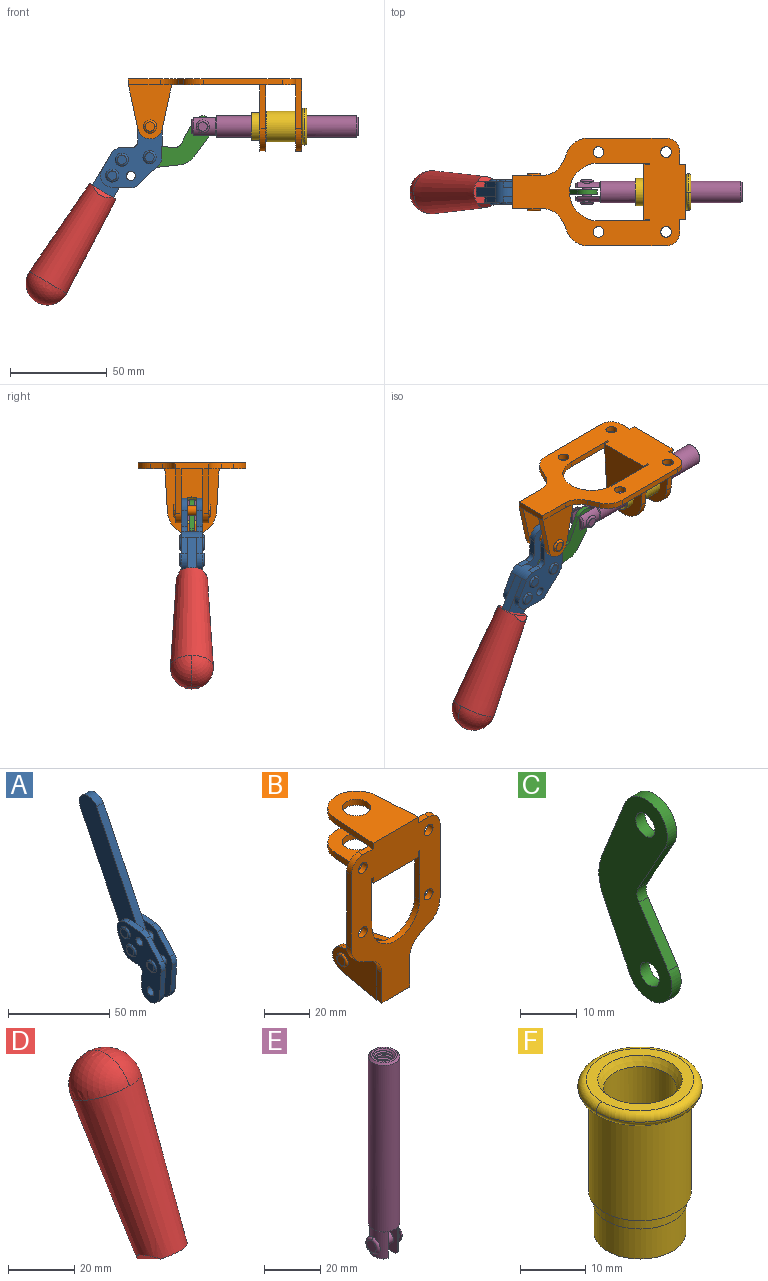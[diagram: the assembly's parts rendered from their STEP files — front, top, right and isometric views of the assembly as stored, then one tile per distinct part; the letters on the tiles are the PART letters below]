
ASSEMBLY  parts=6 mates=6
PART A: 59 faces, bbox 12.9x60.2x99.6 mm
  f0: torus R=2.39mm, axis (-1,0,0), area 14.9mm2, adj f20,f43,f51
  f1: torus R=2.39mm, axis (-1,0,0), area 14.9mm2, adj f19,f42,f51
  f2: torus R=2.39mm, axis (-1,0,0), area 14.9mm2, adj f18,f35,f51
  f3: torus R=2.39mm, axis (-1,0,0), area 14.9mm2, adj f14,f17,f23
  f4: torus R=2.39mm, axis (-1,0,0), area 14.9mm2, adj f13,f16,f23
  f5: torus R=2.39mm, axis (-1,0,0), area 14.9mm2, adj f12,f15,f23
  f6: cylinder r=2.39mm len=4.78mm, axis (1,0,0), area 46.5mm2, adj f48,f50,f51
  f7: cylinder r=2.39mm len=4.78mm, axis (1,0,0), area 46.5mm2, adj f50,f51
  f8: cylinder r=6.35mm len=12.68mm, axis (1,0,0), area 61.8mm2, adj f38,f39,f50,f51
  f9: cylinder r=2.39mm len=4.78mm, axis (-1,0,0), area 70.5mm2, adj f46,f50
  f10: cylinder r=2.39mm len=4.78mm, axis (-1,0,0), area 46.5mm2, adj f23,f45,f46
  f11: cylinder r=2.39mm len=4.78mm, axis (-1,0,0), area 46.5mm2, adj f23,f46
  f12: plane 4.78x4.78mm, normal (1,0,0), area 17.9mm2, adj f5,f15
  f13: plane 4.78x4.78mm, normal (1,0,0), area 17.9mm2, adj f4,f16
  f14: plane 4.78x4.78mm, normal (1,0,0), area 17.9mm2, adj f3,f17
  f15: torus R=2.39mm, axis (-1,0,0), area 14.9mm2, adj f5,f12,f23
  f16: torus R=2.39mm, axis (-1,0,0), area 14.9mm2, adj f4,f13,f23
  f17: torus R=2.39mm, axis (-1,0,0), area 14.9mm2, adj f3,f14,f23
  f18: plane 4.78x4.78mm, normal (-1,0,0), area 17.9mm2, adj f2,f35
  f19: plane 4.78x4.78mm, normal (-1,0,0), area 17.9mm2, adj f1,f42
  f20: plane 4.78x4.78mm, normal (-1,0,0), area 17.9mm2, adj f0,f43
  f21: plane 2.26x0.2mm, normal (1,0,0), area 0.2mm2, adj f31,f44
  f22: plane 2.26x0.2mm, normal (-1,0,0), area 0.2mm2, adj f41,f44
  f23: plane 39.37x30.77mm, normal (1,0,0), area 565.5mm2, adj f3,f4,f5,f10,f11,f15,f16,f17
  f24: cylinder r=6.1mm len=4.15mm, axis (-1,0,0), area 14.7mm2, adj f23,f25,f32,f46
  f25: plane 10.25x9.01mm, normal (0,-0.75,0.66), area 42.3mm2, adj f23,f24,f26,f46
  f26: cylinder r=6.35mm len=4.64mm, axis (-1,0,0), area 15.6mm2, adj f23,f25,f27,f46
  f27: plane 15.84x3.1mm, normal (0,-1,-0.07), area 49.2mm2, adj f23,f26,f28,f46
  f28: cylinder r=6.35mm len=12.68mm, axis (-1,0,0), area 61.8mm2, adj f23,f27,f29,f46
  f29: plane 8.11x3.1mm, normal (0,1,0.07), area 25.2mm2, adj f23,f28,f30,f46
  f30: cylinder r=3.05mm len=3.25mm, axis (-1,0,0), area 14.8mm2, adj f23,f29,f31,f46
  f31: plane 5.99x3.1mm, normal (0,0.07,-1), area 18.6mm2, adj f21,f23,f30,f44,f46
  f32: plane 9.5x3.1mm, normal (0,-0.07,1), area 29.5mm2, adj f23,f24,f33,f46,f47
  f33: cylinder r=6.1mm len=8.63mm, axis (-1,0,0), area 39.1mm2, adj f23,f32,f34,f47
  f34: plane 8.65x3.96mm, normal (0,0.91,-0.42), area 29.5mm2, adj f23,f33,f44,f47
  f35: torus R=2.39mm, axis (-1,0,0), area 14.9mm2, adj f2,f18,f51
  f36: plane 10.25x9.01mm, normal (0,-0.75,0.66), area 42.3mm2, adj f37,f49,f50,f51
  f37: cylinder r=6.35mm len=4.64mm, axis (1,0,0), area 15.6mm2, adj f36,f38,f50,f51
  f38: plane 15.84x3.1mm, normal (0,-1,-0.07), area 49.2mm2, adj f8,f37,f50,f51
  f39: plane 8.11x3.1mm, normal (0,1,0.07), area 25.2mm2, adj f8,f40,f50,f51
  f40: cylinder r=3.05mm len=3.25mm, axis (1,0,0), area 14.8mm2, adj f39,f41,f50,f51
  f41: plane 5.99x3.1mm, normal (0,0.07,-1), area 18.6mm2, adj f22,f40,f44,f50,f51
  f42: torus R=2.39mm, axis (-1,0,0), area 14.9mm2, adj f1,f19,f51
  f43: torus R=2.39mm, axis (-1,0,0), area 14.9mm2, adj f0,f20,f51
  f44: cylinder r=6.35mm len=12.12mm, axis (-1,0,0), area 128.9mm2, adj f21,f22,f23,f31,f34,f41,f46,f47
  f45: plane 2.65x1.35mm, normal (1,0,0), area 1mm2, adj f10,f55
  f46: plane 39.08x20.42mm, normal (-1,0,0), area 412.5mm2, adj f9,f10,f11,f24,f25,f26,f27,f28
  f47: plane 77.62x39.82mm, normal (1,0,0), area 850mm2, adj f32,f33,f34,f44,f53,f54,f55
  f48: plane 2.65x1.35mm, normal (-1,0,0), area 1mm2, adj f6,f55
  f49: cylinder r=6.1mm len=4.15mm, axis (1,0,0), area 14.7mm2, adj f36,f50,f51,f56
  f50: plane 39.08x20.42mm, normal (1,0,0), area 412.5mm2, adj f6,f7,f8,f9,f36,f37,f38,f39
  f51: plane 39.37x30.77mm, normal (-1,0,0), area 565.5mm2, adj f0,f1,f2,f6,f7,f8,f35,f36
  f52: plane 8.65x3.96mm, normal (0,0.91,-0.42), area 29.5mm2, adj f44,f51,f57,f58
  f53: plane 68.49x33.4mm, normal (0,0.9,-0.44), area 358.1mm2, adj f44,f47,f54,f58
  f54: cylinder r=6.35mm len=12.06mm, axis (1,0,0), area 93.7mm2, adj f47,f53,f55,f58
  f55: plane 68.49x33.4mm, normal (0,-0.9,0.44), area 358.1mm2, adj f44,f45,f46,f47,f48,f50,f54,f58
  f56: plane 9.5x3.1mm, normal (0,-0.07,1), area 29.5mm2, adj f49,f50,f51,f57,f58
  f57: cylinder r=6.1mm len=8.63mm, axis (1,0,0), area 39.1mm2, adj f51,f52,f56,f58
  f58: plane 77.62x39.82mm, normal (-1,0,0), area 850mm2, adj f44,f52,f53,f54,f55,f56,f57
PART B: 55 faces, bbox 55.7x37.4x89.8 mm
  f0: torus R=2.41mm, axis (-1,0,0), area 15mm2, adj f11,f15,f25
  f1: torus R=2.41mm, axis (-1,0,0), area 15mm2, adj f10,f12,f22
  f2: cylinder r=2.78mm len=5.56mm, axis (0,-1,0), area 54.2mm2, adj f30,f54
  f3: cylinder r=14.99mm len=29.97mm, axis (0,-1,0), area 145.9mm2, adj f30,f49,f53,f54
  f4: cylinder r=2.78mm len=5.56mm, axis (0,-1,0), area 54.2mm2, adj f30,f54
  f5: cylinder r=2.78mm len=5.56mm, axis (0,-1,0), area 54.2mm2, adj f30,f54
  f6: cylinder r=2.78mm len=5.56mm, axis (0,-1,0), area 54.2mm2, adj f30,f54
  f7: cylinder r=6.35mm len=12.7mm, axis (0,0,1), area 123.6mm2, adj f27,f51
  f8: cylinder r=6.35mm len=12.7mm, axis (0,0,-1), area 124.7mm2, adj f21,f35
  f9: cylinder r=2.41mm len=11.18mm, axis (-1,0,0), area 169.4mm2, adj f16,f19
  f10: plane 4.83x4.83mm, normal (1,0,0), area 18.3mm2, adj f1,f12
  f11: plane 4.83x4.83mm, normal (-1,0,0), area 18.3mm2, adj f0,f15
  f12: torus R=2.41mm, axis (-1,0,0), area 15mm2, adj f1,f10,f22
  f13: cylinder r=6.35mm len=12.41mm, axis (1,0,0), area 53.4mm2, adj f18,f19,f22,f23
  f14: cylinder r=6.35mm len=12.41mm, axis (-1,0,0), area 53.4mm2, adj f16,f17,f24,f25
  f15: torus R=2.41mm, axis (-1,0,0), area 15mm2, adj f0,f11,f25
  f16: plane 27.86x22.35mm, normal (1,0,0), area 425.4mm2, adj f9,f14,f17,f24,f30
  f17: plane 22.86x4.97mm, normal (0,0.21,0.98), area 72.5mm2, adj f14,f16,f25,f30
  f18: plane 22.86x4.97mm, normal (0,0.21,0.98), area 72.5mm2, adj f13,f19,f22,f30
  f19: plane 27.86x22.35mm, normal (-1,0,0), area 425.4mm2, adj f9,f13,f18,f23,f30
  f20: cylinder r=12.7mm len=25.35mm, axis (0,0,-1), area 119.8mm2, adj f21,f34,f35,f36
  f21: plane 34.21x28.07mm, normal (0,0,-1), area 702.4mm2, adj f8,f20,f30,f34,f36
  f22: plane 27.96x22.45mm, normal (1,0,0), area 407.2mm2, adj f1,f12,f13,f18,f23,f30,f42,f43
  f23: plane 22.86x4.97mm, normal (0,0.21,-0.98), area 72.5mm2, adj f13,f19,f22,f44
  f24: plane 22.86x4.97mm, normal (0,0.21,-0.98), area 72.5mm2, adj f14,f16,f25,f44
  f25: plane 27.86x22.35mm, normal (-1,0,0), area 407.1mm2, adj f0,f14,f15,f17,f24,f30,f45,f46
  f26: plane 3.1x0.95mm, normal (0,0,-1), area 2.7mm2, adj f30,f49,f50,f54
  f27: plane 34.21x28.07mm, normal (0,0,1), area 702.4mm2, adj f7,f28,f30,f50,f52
  f28: cylinder r=12.7mm len=25.35mm, axis (0,0,1), area 118.8mm2, adj f27,f50,f51,f52
  f29: plane 3.1x0.95mm, normal (0,0,-1), area 2.7mm2, adj f30,f52,f53,f54
  f30: plane 86.54x55.63mm, normal (0,1,0), area 2362.9mm2, adj f2,f3,f4,f5,f6,f16,f17,f18
  f31: plane 40.56x3.1mm, normal (-1,0,0), area 125.7mm2, adj f30,f32,f48,f54
  f32: cylinder r=7.11mm len=7.11mm, axis (0,-1,0), area 34.6mm2, adj f30,f31,f33,f54
  f33: plane 6.67x3.1mm, normal (0,0,1), area 20.4mm2, adj f30,f32,f34,f54
  f34: plane 25.39x3.13mm, normal (-1,0.06,0), area 79.5mm2, adj f20,f21,f33,f35,f54
  f35: plane 37.31x28.45mm, normal (0,0,1), area 789.9mm2, adj f8,f20,f34,f36,f54
  f36: plane 25.39x3.13mm, normal (1,0.06,0), area 79.5mm2, adj f20,f21,f35,f37,f54
  f37: plane 6.67x3.1mm, normal (0,0,1), area 20.4mm2, adj f30,f36,f38,f54
  f38: cylinder r=7.11mm len=7.11mm, axis (0,-1,0), area 34.6mm2, adj f30,f37,f39,f54
  f39: plane 40.56x3.1mm, normal (1,0,0), area 125.7mm2, adj f30,f38,f40,f54
  f40: cylinder r=11.18mm len=10.16mm, axis (0,-1,0), area 39.5mm2, adj f30,f39,f41,f54
  f41: plane 6.09x3.1mm, normal (0.42,0,-0.91), area 20.8mm2, adj f30,f40,f42,f54
  f42: cylinder r=11.18mm len=9.41mm, axis (0,-1,0), area 37.2mm2, adj f22,f30,f41,f43,f54
  f43: plane 16.5x3.1mm, normal (1,0,0), area 51.1mm2, adj f22,f42,f44,f54
  f44: plane 17.37x3.1mm, normal (0,0,-1), area 53.8mm2, adj f23,f24,f30,f43,f45,f54
  f45: plane 16.5x3.1mm, normal (-1,0,0), area 51.1mm2, adj f25,f44,f46,f54
  f46: cylinder r=11.18mm len=9.41mm, axis (0,-1,0), area 37.2mm2, adj f25,f30,f45,f47,f54
  f47: plane 6.09x3.1mm, normal (-0.42,0,-0.91), area 20.8mm2, adj f30,f46,f48,f54
  f48: cylinder r=11.18mm len=10.16mm, axis (0,-1,0), area 39.5mm2, adj f30,f31,f47,f54
  f49: plane 26.54x3.1mm, normal (-1,0,0), area 82.3mm2, adj f3,f26,f30,f54
  f50: plane 25.39x3.1mm, normal (1,0.06,0), area 78.8mm2, adj f26,f27,f28,f51,f54
  f51: plane 37.31x28.45mm, normal (0,0,-1), area 789.9mm2, adj f7,f28,f50,f52,f54
  f52: plane 25.39x3.1mm, normal (-1,0.06,0), area 78.8mm2, adj f27,f28,f29,f51,f54
  f53: plane 26.54x3.1mm, normal (1,0,0), area 82.3mm2, adj f3,f29,f30,f54
  f54: plane 89.66x55.63mm, normal (0,-1,0), area 2678.5mm2, adj f2,f3,f4,f5,f6,f26,f29,f31
PART C: 12 faces, bbox 2.3x18.2x42.8 mm
  f0: cylinder r=2.4mm len=4.8mm, axis (1,0,0), area 34.9mm2, adj f4,f11
  f1: cylinder r=10.41mm len=8.47mm, axis (1,0,0), area 20.2mm2, adj f4,f9,f10,f11
  f2: cylinder r=3.05mm len=3.16mm, axis (1,0,0), area 7.7mm2, adj f4,f6,f7,f11
  f3: cylinder r=2.4mm len=4.8mm, axis (1,0,0), area 34.9mm2, adj f4,f11
  f4: plane 42.81x18.23mm, normal (-1,0,0), area 414.1mm2, adj f0,f1,f2,f3,f5,f6,f7,f8
  f5: cylinder r=5.54mm len=10.67mm, axis (1,0,0), area 41.8mm2, adj f4,f6,f10,f11
  f6: plane 11.66x6.53mm, normal (0,-0.87,-0.49), area 30.9mm2, adj f2,f4,f5,f11
  f7: plane 11.17x7.33mm, normal (0,-0.84,0.55), area 30.9mm2, adj f2,f4,f8,f11
  f8: cylinder r=5.54mm len=10.51mm, axis (1,0,0), area 41.8mm2, adj f4,f7,f9,f11
  f9: plane 13.67x6.67mm, normal (0,0.9,-0.44), area 35.1mm2, adj f1,f4,f8,f11
  f10: plane 14.1x5.7mm, normal (0,0.93,0.37), area 35.1mm2, adj f1,f4,f5,f11
  f11: plane 42.81x18.23mm, normal (1,0,0), area 414.1mm2, adj f0,f1,f2,f3,f5,f6,f7,f8
PART D: 11 faces, bbox 22.3x42.6x64.5 mm
  f0: sphere r=11.13mm, area 411.4mm2, adj f1,f8
  f1: cone r=11.11mm half-angle=3.3deg, axis (0,0.44,0.9), area 3251.8mm2, adj f0,f7,f8,f9,f10
  f2: cylinder r=6.16mm len=11.7mm, axis (1,0,0), area 89.5mm2, adj f3,f4,f5,f6
  f3: plane 60.23x36.75mm, normal (-1,0,0), area 763.6mm2, adj f2,f4,f6,f10
  f4: plane 51.37x25.05mm, normal (0,0.9,-0.44), area 264.2mm2, adj f2,f3,f5,f10
  f5: plane 60.23x36.75mm, normal (1,0,0), area 763.6mm2, adj f2,f4,f6,f10
  f6: plane 51.37x25.05mm, normal (0,-0.9,0.44), area 264.2mm2, adj f2,f3,f5,f10
  f7: plane 9.95x5.95mm, normal (0.71,-0.31,-0.64), area 25.8mm2, adj f1,f10
  f8: sphere r=11.13mm, area 411.4mm2, adj f0,f1
  f9: plane 9.95x5.95mm, normal (-0.71,-0.31,-0.64), area 25.8mm2, adj f1,f10
  f10: plane 14.27x11.38mm, normal (0,-0.44,-0.9), area 106.7mm2, adj f1,f3,f4,f5,f6,f7,f9
PART E: 48 faces, bbox 12.6x11.1x86.1 mm
  f0: torus R=2.41mm, axis (-1,0,0), area 15mm2, adj f30,f32,f34
  f1: torus R=2.41mm, axis (-1,0,0), area 15mm2, adj f29,f31,f33
  f2: cylinder r=5.54mm len=72.39mm, axis (0,0,1), area 2518.5mm2, adj f3,f4,f42,f43
  f3: cone r=5.54mm half-angle=45deg, axis (0,0,1), area 7.6mm2, adj f2,f5,f41
  f4: cone r=5.54mm half-angle=45deg, axis (0,0,-1), area 34.9mm2, adj f2,f39
  f5: cylinder r=5.08mm len=11.48mm, axis (0,0,1), area 108.3mm2, adj f3,f7,f8,f41
  f6: cylinder r=2.41mm len=4.83mm, axis (-1,0,0), area 71.2mm2, adj f40,f41
  f7: cylinder r=2.41mm len=4.83mm, axis (-1,0,0), area 7.6mm2, adj f5,f34
  f8: cone r=5.08mm half-angle=45deg, axis (0,0,1), area 10.6mm2, adj f5,f37,f41
  f9: cone r=3.98mm half-angle=45deg, axis (0,0,1), area 17.6mm2, adj f27,f39,f45,f46,f47
  f10: cylinder r=2.41mm len=4.83mm, axis (-1,0,0), area 7.6mm2, adj f33,f38
  f11: cylinder r=3.2mm len=6.4mm, axis (0,0,1), area 78.4mm2, adj f12,f28,f44,f45,f47
  f12: cylinder r=3.2mm len=6.4mm, axis (0,0,1), area 10.5mm2, adj f11,f13,f45,f47
  f13: cylinder r=3.2mm len=6.4mm, axis (0,0,1), area 10.5mm2, adj f12,f14,f45,f47
  f14: cylinder r=3.2mm len=6.4mm, axis (0,0,1), area 10.5mm2, adj f13,f15,f45,f47
  f15: cylinder r=3.2mm len=6.4mm, axis (0,0,1), area 10.5mm2, adj f14,f16,f45,f47
  f16: cylinder r=3.2mm len=6.4mm, axis (0,0,1), area 10.5mm2, adj f15,f17,f45,f47
  f17: cylinder r=3.2mm len=6.4mm, axis (0,0,1), area 10.5mm2, adj f16,f18,f45,f47
  f18: cylinder r=3.2mm len=6.4mm, axis (0,0,1), area 10.5mm2, adj f17,f19,f45,f47
  f19: cylinder r=3.2mm len=6.4mm, axis (0,0,1), area 10.5mm2, adj f18,f20,f45,f47
  f20: cylinder r=3.2mm len=6.4mm, axis (0,0,1), area 10.5mm2, adj f19,f21,f45,f47
  f21: cylinder r=3.2mm len=6.4mm, axis (0,0,1), area 10.5mm2, adj f20,f22,f45,f47
  f22: cylinder r=3.2mm len=6.4mm, axis (0,0,1), area 10.5mm2, adj f21,f23,f45,f47
  f23: cylinder r=3.2mm len=6.4mm, axis (0,0,1), area 10.5mm2, adj f22,f24,f45,f47
  f24: cylinder r=3.2mm len=6.4mm, axis (0,0,1), area 10.5mm2, adj f23,f25,f45,f47
  f25: cylinder r=3.2mm len=6.4mm, axis (0,0,1), area 10.5mm2, adj f24,f26,f45,f47
  f26: cylinder r=3.2mm len=6.4mm, axis (0,0,1), area 10.5mm2, adj f25,f27,f45,f47
  f27: cylinder r=3.2mm len=6.4mm, axis (0,0,1), area 7.4mm2, adj f9,f26,f45,f47
  f28: cone r=3.2mm half-angle=60deg, axis (0,0,1), area 37.2mm2, adj f11
  f29: plane 4.83x4.83mm, normal (-1,0,0), area 18.3mm2, adj f1,f31
  f30: plane 4.83x4.83mm, normal (1,0,0), area 18.3mm2, adj f0,f32
  f31: torus R=2.41mm, axis (-1,0,0), area 15mm2, adj f1,f29,f33
  f32: torus R=2.41mm, axis (-1,0,0), area 15mm2, adj f0,f30,f34
  f33: plane 6.83x6.83mm, normal (1,0,0), area 18.3mm2, adj f1,f10,f31
  f34: plane 6.83x6.83mm, normal (-1,0,0), area 18.3mm2, adj f0,f7,f32
  f35: cone r=5.08mm half-angle=45deg, axis (0,0,1), area 10.6mm2, adj f36,f38,f40
  f36: plane 7.25x1.97mm, normal (0,0,-1), area 10mm2, adj f35,f40
  f37: plane 7.25x1.97mm, normal (0,0,-1), area 10mm2, adj f8,f41
  f38: cylinder r=5.08mm len=11.48mm, axis (0,0,1), area 108.3mm2, adj f10,f35,f40,f42
  f39: plane 9.55x9.55mm, normal (0,0,1), area 22mm2, adj f4,f9
  f40: plane 12.76x10.09mm, normal (1,0,0), area 95.7mm2, adj f6,f35,f36,f38,f42,f43
  f41: plane 12.76x10.09mm, normal (-1,0,0), area 95.7mm2, adj f3,f5,f6,f8,f37,f43
  f42: cone r=5.54mm half-angle=45deg, axis (0,0,1), area 7.6mm2, adj f2,f38,f40
  f43: plane 11.07x4.7mm, normal (0,0,-1), area 50.4mm2, adj f2,f40,f41
  f44: plane 0.89x0.62mm, normal (-1,0,0), area 0.3mm2, adj f11,f45,f46,f47
  f45: bspline ~24.8x7.63mm, area 266.6mm2, adj f9,f11,f12,f13,f14,f15,f16,f17
  f46: bspline ~24.87x7.63mm, area 73.6mm2, adj f9,f44,f45,f47
  f47: bspline ~24.98x7.63mm, area 272.5mm2, adj f9,f11,f12,f13,f14,f15,f16,f17
PART F: 15 faces, bbox 20.6x20.6x28.7 mm
  f0: torus R=8.26mm, axis (0,0,1), area 56.8mm2, adj f1,f10,f12
  f1: torus R=8.26mm, axis (0,0,1), area 56.8mm2, adj f0,f6,f13
  f2: cylinder r=5.59mm len=25.91mm, axis (0,0,1), area 909.6mm2, adj f3,f4
  f3: cone r=6.86mm half-angle=45deg, axis (0,0,-1), area 70.2mm2, adj f2,f14
  f4: cone r=6.47mm half-angle=30deg, axis (0,0,1), area 66.7mm2, adj f2,f13
  f5: cylinder r=7.04mm len=14.07mm, axis (0,0,1), area 252.6mm2, adj f11,f14
  f6: torus R=8.26mm, axis (0,0,1), area 56.8mm2, adj f1,f12,f13
  f7: cylinder r=7.16mm len=14.33mm, axis (0,0,1), area 91.5mm2, adj f9,f11
  f8: cylinder r=7.86mm len=18.42mm, axis (0,0,1), area 909.6mm2, adj f9,f10
  f9: plane 15.72x15.72mm, normal (0,0,-1), area 33mm2, adj f7,f8
  f10: plane 16.51x16.51mm, normal (0,0,-1), area 19.9mm2, adj f0,f8,f12
  f11: plane 14.33x14.33mm, normal (0,0,-1), area 5.7mm2, adj f5,f7
  f12: torus R=8.26mm, axis (0,0,1), area 56.8mm2, adj f0,f6,f10
  f13: plane 16.51x16.51mm, normal (0,0,1), area 82.7mm2, adj f1,f4,f6
  f14: plane 14.07x14.07mm, normal (0,0,-1), area 7.8mm2, adj f3,f5
PLACE A rot(axis=(0.71,-0.71,-0.03),176.5deg) t=(-10.37,0,-58.73)mm
PLACE B rot(axis=(-0.58,0.58,-0.58),120deg) t=(0,0,0)mm fixed
PLACE C rot(axis=(-0.65,-0.65,0.39),137.3deg) t=(-30.26,0,-11.49)mm
PLACE D rot(axis=(0.71,-0.71,-0.03),176.5deg) t=(-10.37,0.04,-58.73)mm
PLACE E rot(axis=(-0.58,0.58,-0.58),120deg) t=(-20.35,0,0)mm
PLACE F rot(axis=(0.71,0,0.71),180deg) t=(0,24.61,-24.61)mm
MATE revolute C.f5 <-> A.f4  axis (0,1,0) through (-32.37,0,-40.49)mm
MATE revolute B.f0 <-> A.f7  axis (0,1,0) through (-32.09,0,-24.61)mm
MATE slider B.f7 <-> E.f2  axis (1,0,0) through (46.39,0,-24.61)mm
MATE fastened F.f0 <-> B.f7  axis (-1,0,0) through (46.39,0,-24.61)mm
MATE revolute C.f3 <-> E.f6  axis (0,1,0) through (-4.87,0,-24.61)mm
MATE fastened A.f54 <-> D.f2  axis (0,1,0) through (-85.91,2.35,-107.1)mm
